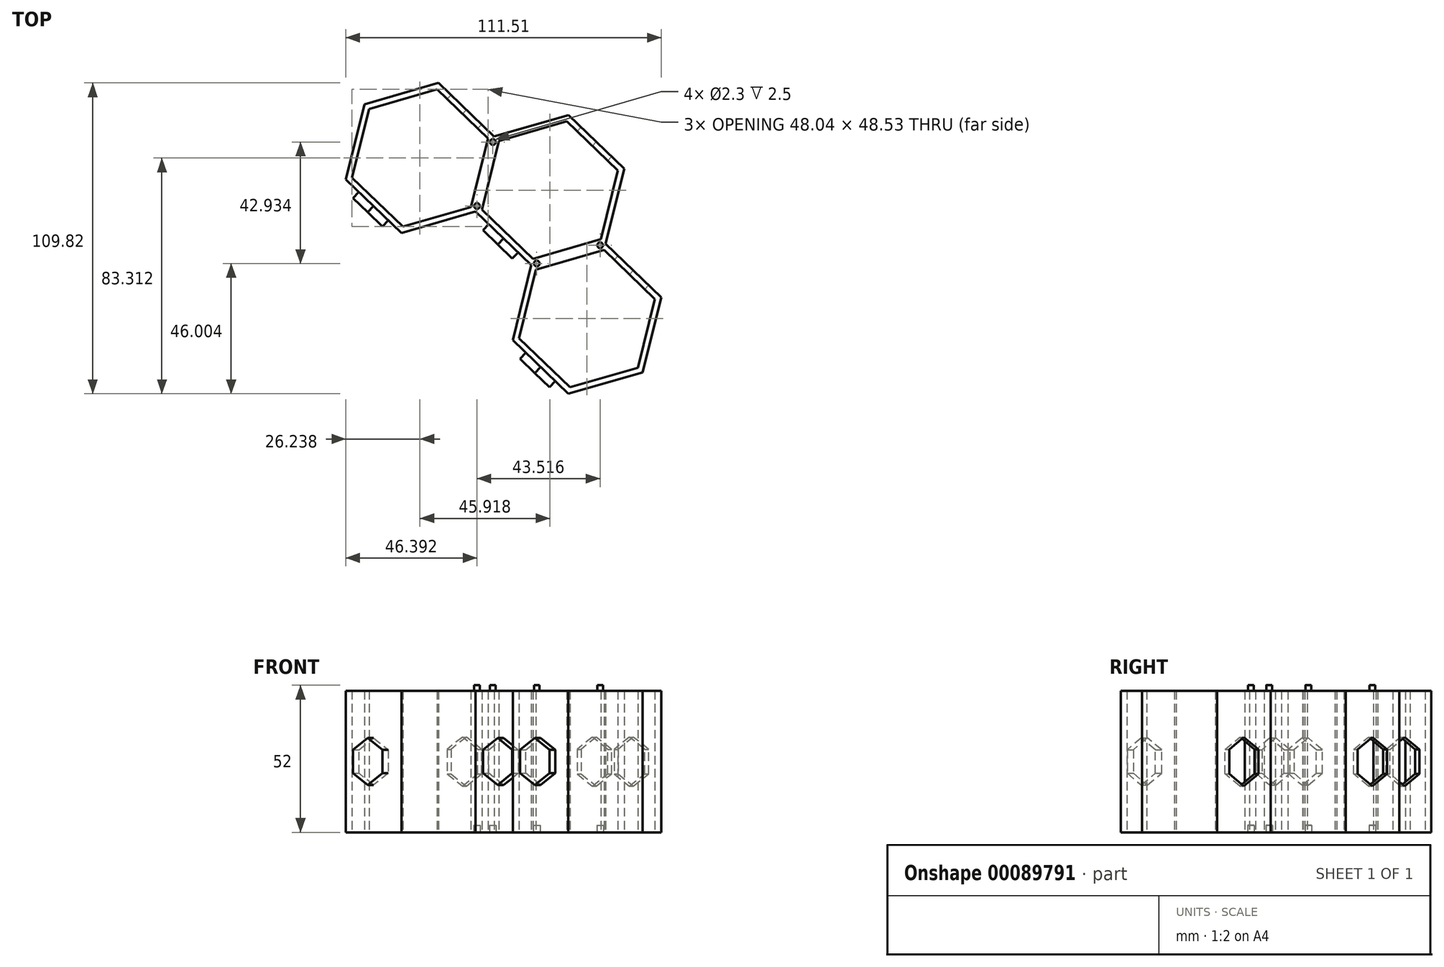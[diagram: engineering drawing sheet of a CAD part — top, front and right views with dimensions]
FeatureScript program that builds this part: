
annotation { "Feature Type Name" : "Feature", "Feature Type Description" : "" }
export const myFeature = defineFeature(function(context is Context, id is Id, definition is map)
    precondition{}
    {
        {
            var Q0;
            Q0=qCreatedBy(makeId("Top.planeOp"),FACE);
            var sketch = newSketch(context, id + "F0", { "sketchPlane" : qUnion([Q0])});
            skCircle(sketch, "E0.cCircle", {"center": v(16.88, 16.02) * mm, "radius": 27.3 * mm, "construction": true});
            skLineSegment(sketch, "E0.0", {"start": v(36.55, -2.92) * mm, "end": v(10.3, -10.5) * mm});
            skLineSegment(sketch, "E0.1", {"start": v(10.3, -10.5) * mm, "end": v(-9.36, 8.45) * mm});
            skLineSegment(sketch, "E0.2", {"start": v(-9.36, 8.45) * mm, "end": v(-2.8, 34.96) * mm});
            skLineSegment(sketch, "E0.3", {"start": v(-2.8, 34.96) * mm, "end": v(23.44, 42.53) * mm});
            skLineSegment(sketch, "E0.4", {"start": v(23.44, 42.53) * mm, "end": v(43.12, 23.58) * mm});
            skLineSegment(sketch, "E0.5", {"start": v(43.12, 23.58) * mm, "end": v(36.55, -2.92) * mm});
            skCircle(sketch, "E1.cCircle", {"center": v(16.88, 16.02) * mm, "radius": 25 * mm, "construction": true});
            skLineSegment(sketch, "E1.0", {"start": v(34.89, -1.32) * mm, "end": v(10.86, -8.25) * mm});
            skLineSegment(sketch, "E1.1", {"start": v(10.86, -8.25) * mm, "end": v(-7.15, 9.1) * mm});
            skLineSegment(sketch, "E1.2", {"start": v(-7.15, 9.1) * mm, "end": v(-1.13, 33.36) * mm});
            skLineSegment(sketch, "E1.3", {"start": v(-1.13, 33.36) * mm, "end": v(22.89, 40.28) * mm});
            skLineSegment(sketch, "E1.4", {"start": v(22.89, 40.28) * mm, "end": v(40.9, 22.94) * mm});
            skLineSegment(sketch, "E1.5", {"start": v(40.9, 22.94) * mm, "end": v(34.89, -1.32) * mm});
            skCircle(sketch, "E2.cCircle", {"center": v(-29.04, 27.37) * mm, "radius": 27.3 * mm, "construction": true});
            skLineSegment(sketch, "E2.0", {"start": v(-9.37, 8.43) * mm, "end": v(-35.6, 0.86) * mm});
            skLineSegment(sketch, "E2.1", {"start": v(-35.6, 0.86) * mm, "end": v(-55.28, 19.8) * mm});
            skLineSegment(sketch, "E2.2", {"start": v(-55.28, 19.8) * mm, "end": v(-48.72, 46.31) * mm});
            skLineSegment(sketch, "E2.3", {"start": v(-48.72, 46.31) * mm, "end": v(-22.48, 53.88) * mm});
            skLineSegment(sketch, "E2.4", {"start": v(-22.48, 53.88) * mm, "end": v(-2.8, 34.94) * mm});
            skLineSegment(sketch, "E2.5", {"start": v(-2.8, 34.94) * mm, "end": v(-9.37, 8.43) * mm});
            skCircle(sketch, "E3.cCircle", {"center": v(-29.04, 27.37) * mm, "radius": 25 * mm, "construction": true});
            skLineSegment(sketch, "E3.0", {"start": v(-11.03, 10.03) * mm, "end": v(-35.05, 3.1) * mm});
            skLineSegment(sketch, "E3.1", {"start": v(-35.05, 3.1) * mm, "end": v(-53.06, 20.45) * mm});
            skLineSegment(sketch, "E3.2", {"start": v(-53.06, 20.45) * mm, "end": v(-47.05, 44.71) * mm});
            skLineSegment(sketch, "E3.3", {"start": v(-47.05, 44.71) * mm, "end": v(-23.03, 51.64) * mm});
            skLineSegment(sketch, "E3.4", {"start": v(-23.03, 51.64) * mm, "end": v(-5.02, 34.3) * mm});
            skLineSegment(sketch, "E3.5", {"start": v(-5.02, 34.3) * mm, "end": v(-11.03, 10.03) * mm});
            skCircle(sketch, "E4.cCircle", {"center": v(29.99, -29.43) * mm, "radius": 27.3 * mm, "construction": true});
            skLineSegment(sketch, "E4.0", {"start": v(49.66, -48.37) * mm, "end": v(23.42, -55.94) * mm});
            skLineSegment(sketch, "E4.1", {"start": v(23.42, -55.94) * mm, "end": v(3.75, -37) * mm});
            skLineSegment(sketch, "E4.2", {"start": v(3.75, -37) * mm, "end": v(10.31, -10.49) * mm});
            skLineSegment(sketch, "E4.3", {"start": v(10.31, -10.49) * mm, "end": v(36.55, -2.92) * mm});
            skLineSegment(sketch, "E4.4", {"start": v(36.55, -2.92) * mm, "end": v(56.23, -21.86) * mm});
            skLineSegment(sketch, "E4.5", {"start": v(56.23, -21.86) * mm, "end": v(49.66, -48.37) * mm});
            skCircle(sketch, "E5.cCircle", {"center": v(29.99, -29.43) * mm, "radius": 25 * mm, "construction": true});
            skLineSegment(sketch, "E5.0", {"start": v(48, -46.77) * mm, "end": v(23.97, -53.7) * mm});
            skLineSegment(sketch, "E5.1", {"start": v(23.97, -53.7) * mm, "end": v(5.96, -36.36) * mm});
            skLineSegment(sketch, "E5.2", {"start": v(5.96, -36.36) * mm, "end": v(11.98, -12.1) * mm});
            skLineSegment(sketch, "E5.3", {"start": v(11.98, -12.1) * mm, "end": v(36, -5.16) * mm});
            skLineSegment(sketch, "E5.4", {"start": v(36, -5.16) * mm, "end": v(54, -22.5) * mm});
            skLineSegment(sketch, "E5.5", {"start": v(54, -22.5) * mm, "end": v(48, -46.77) * mm});
            skLineSegment(sketch, "E6.0", {"start": v(29.99, -29.43) * mm, "end": v(48, -46.77) * mm, "construction": true});
            skLineSegment(sketch, "E7.0", {"start": v(16.88, 16.02) * mm, "end": v(34.89, -1.32) * mm, "construction": true});
            skLineSegment(sketch, "E8.0", {"start": v(-29.04, 27.37) * mm, "end": v(-11.03, 10.03) * mm, "construction": true});
            skSolve(sketch);
        }
        {
            var Q0;
            {var subQ0=sQuery(id+"F0.wireOp",EDGE,"E0.0");Q0=makeQuery(id+"F0.imprint","IMPRINT",FACE,{"disambiguationData":[TD([[makeQuery(id+"F0.imprint","IMPRINT",EDGE,{"derivedFrom":subQ0}),-1.0]])]});}
            var Q1;
            {var subQ0=sQuery(id+"F0.wireOp",EDGE,"E2.0");Q1=makeQuery(id+"F0.imprint","IMPRINT",FACE,{"disambiguationData":[TD([[makeQuery(id+"F0.imprint","IMPRINT",EDGE,{"derivedFrom":subQ0}),-1.0]])]});}
            var Q2;
            Q2=makeQuery(id+"F0.imprint","IMPRINT",FACE,{"disambiguationData":[TD([[makeQuery(id+"F0.imprint","IMPRINT",EDGE,{"derivedFrom":sQuery(id+"F0.wireOp",EDGE,"E4.0")}),-1.0]])]});
            extrude(context, id + "F1", {"entities" : qUnion([Q0, Q1, Q2]), "depth" : 50 * mm});
        }
        {
            var Q0;
            Q0=makeQuery(id+"F1.opExtrude","CAP_FACE",FACE,{"disambiguationData":[OSD([sQuery(id+"F0.wireOp",EDGE,"E0.0"),sQuery(id+"F0.wireOp",EDGE,"E0.1"),sQuery(id+"F0.wireOp",EDGE,"E0.2"),sQuery(id+"F0.wireOp",EDGE,"E0.3"),sQuery(id+"F0.wireOp",EDGE,"E0.4"),sQuery(id+"F0.wireOp",EDGE,"E0.5"),sQuery(id+"F0.wireOp",EDGE,"E1.0"),sQuery(id+"F0.wireOp",EDGE,"E1.1"),sQuery(id+"F0.wireOp",EDGE,"E1.2"),sQuery(id+"F0.wireOp",EDGE,"E1.3"),sQuery(id+"F0.wireOp",EDGE,"E1.4"),sQuery(id+"F0.wireOp",EDGE,"E1.5"),sQuery(id+"F0.wireOp",EDGE,"E2.0"),sQuery(id+"F0.wireOp",EDGE,"E2.1"),sQuery(id+"F0.wireOp",EDGE,"E2.2"),sQuery(id+"F0.wireOp",EDGE,"E2.3"),sQuery(id+"F0.wireOp",EDGE,"E2.4"),sQuery(id+"F0.wireOp",EDGE,"E2.5"),sQuery(id+"F0.wireOp",EDGE,"E3.0"),sQuery(id+"F0.wireOp",EDGE,"E3.1"),sQuery(id+"F0.wireOp",EDGE,"E3.2"),sQuery(id+"F0.wireOp",EDGE,"E3.3"),sQuery(id+"F0.wireOp",EDGE,"E3.4"),sQuery(id+"F0.wireOp",EDGE,"E3.5"),sQuery(id+"F0.wireOp",EDGE,"E4.0"),sQuery(id+"F0.wireOp",EDGE,"E4.1"),sQuery(id+"F0.wireOp",EDGE,"E4.2"),sQuery(id+"F0.wireOp",EDGE,"E4.3"),sQuery(id+"F0.wireOp",EDGE,"E4.4"),sQuery(id+"F0.wireOp",EDGE,"E4.5"),sQuery(id+"F0.wireOp",EDGE,"E5.0"),sQuery(id+"F0.wireOp",EDGE,"E5.1"),sQuery(id+"F0.wireOp",EDGE,"E5.2"),sQuery(id+"F0.wireOp",EDGE,"E5.3"),sQuery(id+"F0.wireOp",EDGE,"E5.4"),sQuery(id+"F0.wireOp",EDGE,"E5.5")])],"isStart":false});
            var sketch = newSketch(context, id + "F2", { "sketchPlane" : qUnion([Q0])});
            skCircle(sketch, "E9", {"center": v(-3.28, 33) * mm, "radius": 1 * mm});
            skCircle(sketch, "E10", {"center": v(-8.89, 10.37) * mm, "radius": 1 * mm});
            skCircle(sketch, "E11", {"center": v(12.23, -9.94) * mm, "radius": 1 * mm});
            skCircle(sketch, "E12", {"center": v(34.63, -3.48) * mm, "radius": 1 * mm});
            skSolve(sketch);
        }
        {
            var Q0;
            Q0=makeQuery(id+"F1.opExtrude","CAP_FACE",FACE,{"disambiguationData":[OSD([sQuery(id+"F0.wireOp",EDGE,"E0.0"),sQuery(id+"F0.wireOp",EDGE,"E0.1"),sQuery(id+"F0.wireOp",EDGE,"E0.2"),sQuery(id+"F0.wireOp",EDGE,"E0.3"),sQuery(id+"F0.wireOp",EDGE,"E0.4"),sQuery(id+"F0.wireOp",EDGE,"E0.5"),sQuery(id+"F0.wireOp",EDGE,"E1.0"),sQuery(id+"F0.wireOp",EDGE,"E1.1"),sQuery(id+"F0.wireOp",EDGE,"E1.2"),sQuery(id+"F0.wireOp",EDGE,"E1.3"),sQuery(id+"F0.wireOp",EDGE,"E1.4"),sQuery(id+"F0.wireOp",EDGE,"E1.5"),sQuery(id+"F0.wireOp",EDGE,"E2.0"),sQuery(id+"F0.wireOp",EDGE,"E2.1"),sQuery(id+"F0.wireOp",EDGE,"E2.2"),sQuery(id+"F0.wireOp",EDGE,"E2.3"),sQuery(id+"F0.wireOp",EDGE,"E2.4"),sQuery(id+"F0.wireOp",EDGE,"E2.5"),sQuery(id+"F0.wireOp",EDGE,"E3.0"),sQuery(id+"F0.wireOp",EDGE,"E3.1"),sQuery(id+"F0.wireOp",EDGE,"E3.2"),sQuery(id+"F0.wireOp",EDGE,"E3.3"),sQuery(id+"F0.wireOp",EDGE,"E3.4"),sQuery(id+"F0.wireOp",EDGE,"E3.5"),sQuery(id+"F0.wireOp",EDGE,"E4.0"),sQuery(id+"F0.wireOp",EDGE,"E4.1"),sQuery(id+"F0.wireOp",EDGE,"E4.2"),sQuery(id+"F0.wireOp",EDGE,"E4.3"),sQuery(id+"F0.wireOp",EDGE,"E4.4"),sQuery(id+"F0.wireOp",EDGE,"E4.5"),sQuery(id+"F0.wireOp",EDGE,"E5.0"),sQuery(id+"F0.wireOp",EDGE,"E5.1"),sQuery(id+"F0.wireOp",EDGE,"E5.2"),sQuery(id+"F0.wireOp",EDGE,"E5.3"),sQuery(id+"F0.wireOp",EDGE,"E5.4"),sQuery(id+"F0.wireOp",EDGE,"E5.5")])],"isStart":true});
            var sketch = newSketch(context, id + "F3", { "sketchPlane" : qUnion([Q0])});
            skCircle(sketch, "E13", {"center": v(-8.89, -10.37) * mm, "radius": 1.15 * mm});
            skCircle(sketch, "E14", {"center": v(-3.28, -33) * mm, "radius": 1.15 * mm});
            skCircle(sketch, "E15", {"center": v(12.23, 9.94) * mm, "radius": 1.15 * mm});
            skCircle(sketch, "E16", {"center": v(34.63, 3.48) * mm, "radius": 1.15 * mm});
            skSolve(sketch);
        }
        {
            var Q0;
            Q0 = qSketchRegion(id + "F3", true);
            extrude(context, id + "F4", {"entities" : qUnion([Q0]), "operationType" : NewBodyOperationType.REMOVE, "oppositeDirection" : true, "depth" : 2.5 * mm});
        }
        {
            var Q0;
            Q0 = qSketchRegion(id + "F2", true);
            extrude(context, id + "F5", {"entities" : qUnion([Q0]), "operationType" : NewBodyOperationType.ADD, "depth" : 2 * mm});
        }
        {
            var Q0;
            Q0=makeQuery(id+"F1.opExtrude","SWEPT_FACE",FACE,{"disambiguationData":[OSD([sQuery(id+"F0.wireOp",EDGE,"E0.4")])]});
            var sketch = newSketch(context, id + "F6", { "sketchPlane" : qUnion([Q0])});
            skCircle(sketch, "E17.cCircle", {"center": v(-1.05, 25) * mm, "radius": 7.5 * mm, "construction": true});
            skLineSegment(sketch, "E17.0", {"start": v(-8.55, 29.33) * mm, "end": v(-1.05, 33.66) * mm});
            skLineSegment(sketch, "E17.1", {"start": v(-1.05, 33.66) * mm, "end": v(6.45, 29.33) * mm});
            skLineSegment(sketch, "E17.2", {"start": v(6.45, 29.33) * mm, "end": v(6.45, 20.67) * mm});
            skLineSegment(sketch, "E17.3", {"start": v(6.45, 20.67) * mm, "end": v(-1.05, 16.34) * mm});
            skLineSegment(sketch, "E17.4", {"start": v(-1.05, 16.34) * mm, "end": v(-8.55, 20.67) * mm});
            skLineSegment(sketch, "E17.5", {"start": v(-8.55, 20.67) * mm, "end": v(-8.55, 29.33) * mm});
            skPoint(sketch, "E17.0.midPoint", {"position": v(-4.8, 31.5) * mm});
            skLineSegment(sketch, "E18", {"start": v(12.6, 25) * mm, "end": v(-14.7, 25) * mm, "construction": true});
            skSolve(sketch);
        }
        {
            var Q0;
            Q0=makeQuery(id+"F1.opExtrude","SWEPT_FACE",FACE,{"disambiguationData":[OSD([sQuery(id+"F0.wireOp",EDGE,"E4.4")])]});
            var sketch = newSketch(context, id + "F7", { "sketchPlane" : qUnion([Q0])});
            skLineSegment(sketch, "E19", {"start": v(53.56, 25) * mm, "end": v(26.26, 25) * mm, "construction": true});
            skCircle(sketch, "E20.cCircle", {"center": v(39.91, 25) * mm, "radius": 7.5 * mm, "construction": true});
            skLineSegment(sketch, "E20.0", {"start": v(32.41, 20.67) * mm, "end": v(32.41, 29.33) * mm});
            skLineSegment(sketch, "E20.1", {"start": v(32.41, 29.33) * mm, "end": v(39.91, 33.66) * mm});
            skLineSegment(sketch, "E20.2", {"start": v(39.91, 33.66) * mm, "end": v(47.41, 29.33) * mm});
            skLineSegment(sketch, "E20.3", {"start": v(47.41, 29.33) * mm, "end": v(47.41, 20.67) * mm});
            skLineSegment(sketch, "E20.4", {"start": v(47.41, 20.67) * mm, "end": v(39.91, 16.34) * mm});
            skLineSegment(sketch, "E20.5", {"start": v(39.91, 16.34) * mm, "end": v(32.41, 20.67) * mm});
            skPoint(sketch, "E20.0.midPoint", {"position": v(32.41, 25) * mm});
            skCircle(sketch, "E21.cCircle", {"center": v(-42.01, 25) * mm, "radius": 7.5 * mm, "construction": true});
            skLineSegment(sketch, "E21.0", {"start": v(-49.51, 20.67) * mm, "end": v(-49.51, 29.33) * mm});
            skLineSegment(sketch, "E21.1", {"start": v(-49.51, 29.33) * mm, "end": v(-42.01, 33.66) * mm});
            skLineSegment(sketch, "E21.2", {"start": v(-42.01, 33.66) * mm, "end": v(-34.51, 29.33) * mm});
            skLineSegment(sketch, "E21.3", {"start": v(-34.51, 29.33) * mm, "end": v(-34.51, 20.67) * mm});
            skLineSegment(sketch, "E21.4", {"start": v(-34.51, 20.67) * mm, "end": v(-42.01, 16.34) * mm});
            skLineSegment(sketch, "E21.5", {"start": v(-42.01, 16.34) * mm, "end": v(-49.51, 20.67) * mm});
            skPoint(sketch, "E21.0.midPoint", {"position": v(-49.51, 25) * mm});
            skLineSegment(sketch, "E22", {"start": v(-28.36, 25) * mm, "end": v(-55.67, 25) * mm, "construction": true});
            skSolve(sketch);
        }
        {
            var Q0;
            Q0 = qSketchRegion(id + "F6", true);
            var Q1;
            Q1 = qSketchRegion(id + "F7", true);
            extrude(context, id + "F8", {"entities" : qUnion([Q0, Q1]), "operationType" : NewBodyOperationType.REMOVE, "oppositeDirection" : true, "depth" : 4 * mm});
        }
        {
            var Q0;
            Q0=makeQuery(id+"F1.opExtrude","SWEPT_FACE",FACE,{"disambiguationData":[OSD([sQuery(id+"F0.wireOp",EDGE,"E4.1")])]});
            var sketch = newSketch(context, id + "F9", { "sketchPlane" : qUnion([Q0])});
            skCircle(sketch, "E23.cCircle", {"center": v(42.01, 25) * mm, "radius": 7.2 * mm, "construction": true});
            skLineSegment(sketch, "E23.0", {"start": v(49.21, 29.16) * mm, "end": v(49.21, 20.84) * mm});
            skLineSegment(sketch, "E23.1", {"start": v(49.21, 20.84) * mm, "end": v(42.01, 16.69) * mm});
            skLineSegment(sketch, "E23.2", {"start": v(42.01, 16.69) * mm, "end": v(34.81, 20.84) * mm});
            skLineSegment(sketch, "E23.3", {"start": v(34.81, 20.84) * mm, "end": v(34.81, 29.16) * mm});
            skLineSegment(sketch, "E23.4", {"start": v(34.81, 29.16) * mm, "end": v(42.01, 33.31) * mm});
            skLineSegment(sketch, "E23.5", {"start": v(42.01, 33.31) * mm, "end": v(49.21, 29.16) * mm});
            skPoint(sketch, "E23.0.midPoint", {"position": v(49.21, 25) * mm});
            skCircle(sketch, "E24.cCircle", {"center": v(-39.9, 25) * mm, "radius": 7.2 * mm, "construction": true});
            skLineSegment(sketch, "E24.0", {"start": v(-32.7, 29.16) * mm, "end": v(-32.7, 20.84) * mm});
            skLineSegment(sketch, "E24.1", {"start": v(-32.7, 20.84) * mm, "end": v(-39.9, 16.69) * mm});
            skLineSegment(sketch, "E24.2", {"start": v(-39.9, 16.69) * mm, "end": v(-47.1, 20.84) * mm});
            skLineSegment(sketch, "E24.3", {"start": v(-47.1, 20.84) * mm, "end": v(-47.1, 29.16) * mm});
            skLineSegment(sketch, "E24.4", {"start": v(-47.1, 29.16) * mm, "end": v(-39.9, 33.31) * mm});
            skLineSegment(sketch, "E24.5", {"start": v(-39.9, 33.31) * mm, "end": v(-32.7, 29.16) * mm});
            skPoint(sketch, "E24.0.midPoint", {"position": v(-32.7, 25) * mm});
            skPoint(sketch, "E25", {"position": v(28.36, 25) * mm});
            skLineSegment(sketch, "E26", {"start": v(28.36, 25) * mm, "end": v(55.67, 25) * mm, "construction": true});
            skLineSegment(sketch, "E27", {"start": v(-53.56, 25) * mm, "end": v(-26.25, 25) * mm, "construction": true});
            skSolve(sketch);
        }
        {
            var Q0;
            Q0=makeQuery(id+"F1.opExtrude","SWEPT_FACE",FACE,{"disambiguationData":[OSD([sQuery(id+"F0.wireOp",EDGE,"E0.1")])]});
            var sketch = newSketch(context, id + "F10", { "sketchPlane" : qUnion([Q0])});
            skLineSegment(sketch, "E28", {"start": v(-12.6, 25) * mm, "end": v(14.7, 25) * mm, "construction": true});
            skCircle(sketch, "E29.cCircle", {"center": v(1.05, 25) * mm, "radius": 7.2 * mm, "construction": true});
            skLineSegment(sketch, "E29.0", {"start": v(8.25, 29.16) * mm, "end": v(8.25, 20.84) * mm});
            skLineSegment(sketch, "E29.1", {"start": v(8.25, 20.84) * mm, "end": v(1.05, 16.69) * mm});
            skLineSegment(sketch, "E29.2", {"start": v(1.05, 16.69) * mm, "end": v(-6.15, 20.84) * mm});
            skLineSegment(sketch, "E29.3", {"start": v(-6.15, 20.84) * mm, "end": v(-6.15, 29.16) * mm});
            skLineSegment(sketch, "E29.4", {"start": v(-6.15, 29.16) * mm, "end": v(1.05, 33.31) * mm});
            skLineSegment(sketch, "E29.5", {"start": v(1.05, 33.31) * mm, "end": v(8.25, 29.16) * mm});
            skPoint(sketch, "E29.0.midPoint", {"position": v(8.25, 25) * mm});
            skSolve(sketch);
        }
        {
            var Q0;
            Q0 = qSketchRegion(id + "F10", true);
            var Q1;
            Q1 = qSketchRegion(id + "F9", true);
            extrude(context, id + "F11", {"entities" : qUnion([Q0, Q1]), "depth" : 3 * mm});
        }
    });
